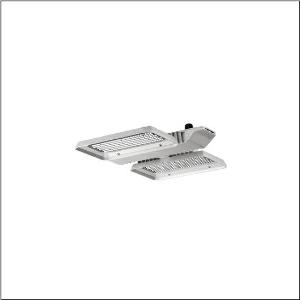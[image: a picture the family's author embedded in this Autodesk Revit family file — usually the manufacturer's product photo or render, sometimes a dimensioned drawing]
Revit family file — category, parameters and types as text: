
# Revit family: highbay_11_51hla1d14fca
name_source: partatom
category: Lighting Fixtures
units: mm (PartAtom-declared; Revit-internal decimal feet)

## family parameters
Cut with Voids When Loaded = No
Host = Face
Light Source = No
Part Type = Normal
Room Calculation Point = No
Round Connector Dimension = Use Diameter
Shared = No

## types (1)
- --- (1 x LED, 14060 lm, 81.2 W, 4000K)
    Apparent Load = 81 VA
    CIE Flux Codes = 88 95 99 100 99
    Color Rendering = 80
    Color Temperature = 4000K
    Default Elevation = 1800 mm
    Description = Highbay 11, LED high bay luminaire, primary light control with lens, of PMMA, light emission: direct distribution, primary light characteristic: symmetric, installation type: surface-mounted, suspended mounting, for 1x 2x LED, rated luminous flux: 14.060lm, luminous efficacy: 173lm/W, light colour: 840, colour temperature: 4000K, control gear: ECG DALI, with terminal, 5-pole, max. 2.5mm², mains connection: 230..240V, AC, 50/60Hz, rated input power: 81W, LED unit, of diecast aluminium, unplated, bead blasted, silver, length: 470mm, width: 500mm, height: 65mm, housing, of diecast aluminium, uncoated, bead blasted, silver, protection rating (complete): IP65, insulation class (complete): insulation class I (protective earthing), certification: CE, ENEC, VDE, UKCA, protection symbol: D, impact resistance: IK08 with glass or PC cover, permissible operating ambient temperature: -35..+55°C, reducing of maximum allowable ambient temperature of 5°C with ceiling mounting, corresponds to IFS (International Featured Standards) requirements for safety and quality in the food industry, packaging unit: 1 piece
    Height = 95 mm
    Lamp = 1 x LED
    Lamp Light Flux = 14060 lm
    Lamp Power = 81.2 W
    Lamp count = 1
    Length = 468 mm
    Luminous efficacy = 173 lm/W
    Manufacturer = Siteco
    ModVariant = No
    Model = 51HLA1D14FCA
    Mounting Place = Ceiling
    Mounting Type = Pendant
    Number of Poles = 1
    OnlyDefault = Yes
    Power Factor = 1
    Product Name = Highbay 11
    Product group = LED high bay luminaire
    ProductGroupID = 903
    Protection Class = Protection class I
    Protection Degree = IP 65
    RLX_Detail_Level = 1
    RLX_Emergency_Light_Flux = 0 lm
    RLX_Emergency_Type = 0
    RLX_Emergency_Type_DB = No
    RlxData = <blob elided: 89749 chars, md5=a1a9f278>
    Socket = socket
    Standby Power = 0 W
    System Light Flux = 14060 lm
    System Power = 81 W
    Type Comments = factory setting: luminous flux: 100 % | dim-lin: 254 | 460 mA
    Type Image = l_1003425.jpg
    URL = http://relux.com
    VarID = @adj_177667
    Voltage = 0 V
    Weight = 0.00 kg
    Width = 501 mm

## geometry (parser evidence)
native form markers: Blend x4, Sweep x12
no freeform markers — native parametric forms only
